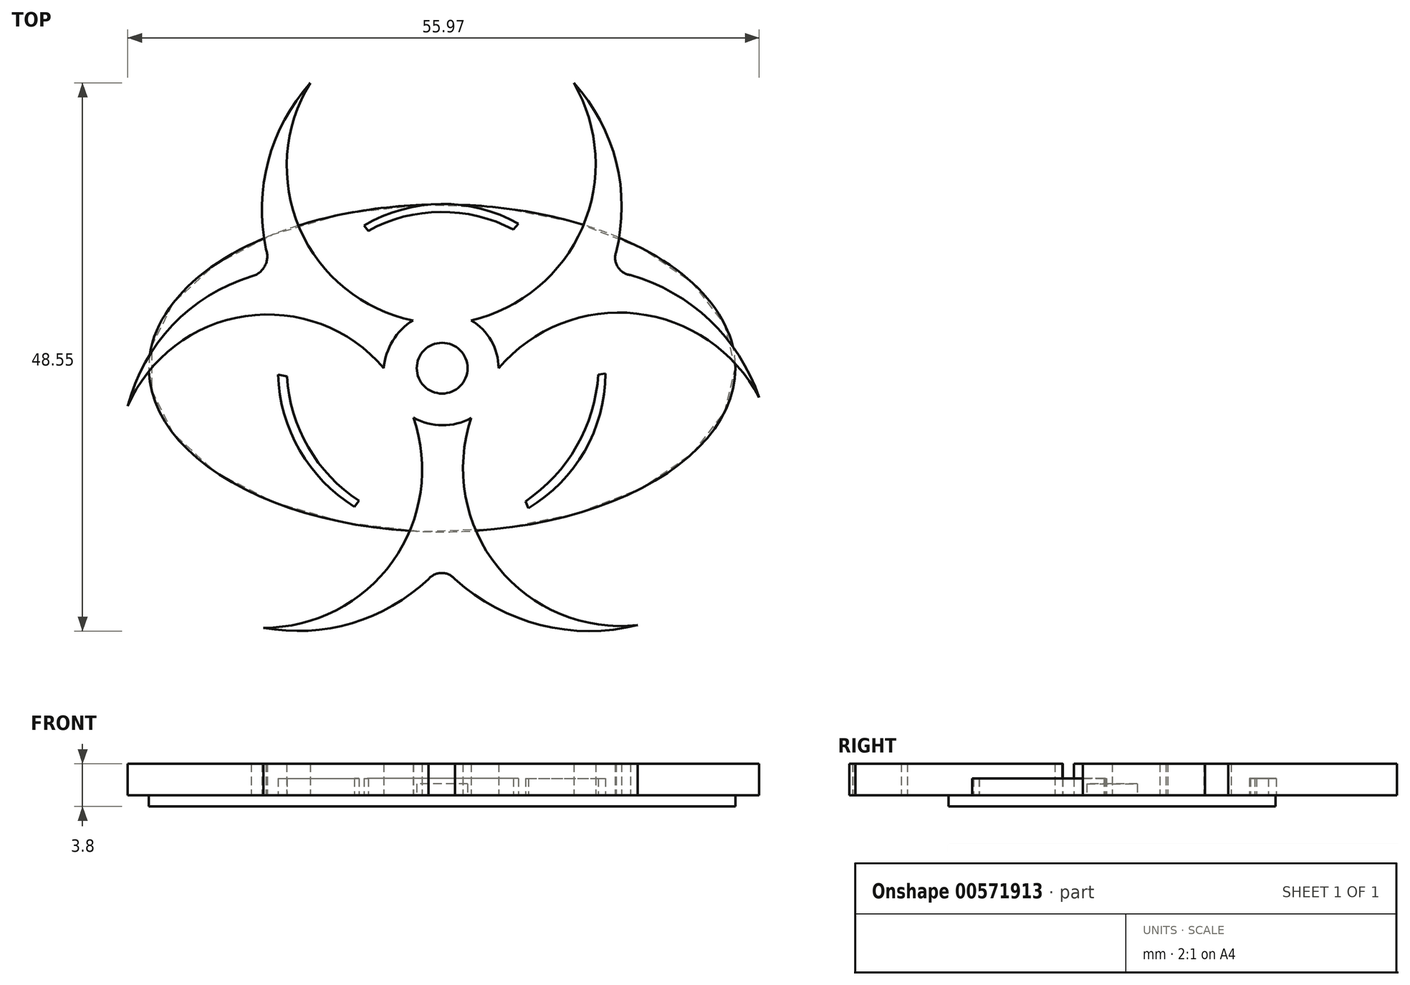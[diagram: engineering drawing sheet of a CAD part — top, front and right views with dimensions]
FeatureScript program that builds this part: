
annotation { "Feature Type Name" : "Feature", "Feature Type Description" : "" }
export const myFeature = defineFeature(function(context is Context, id is Id, definition is map)
    precondition{}
    {
        {
            var Q0;
            Q0=qCreatedBy(makeId("Top.planeOp"),FACE);
            var sketch = newSketch(context, id + "F0", { "sketchPlane" : qUnion([Q0])});
            skCircle(sketch, "E0", {"center": v(0, 0) * mm, "radius": 2.5 * mm});
            skArc(sketch, "E1", {"start": v(-16.91, 8.13) * mm, "mid": v(-15.72, 9.05) * mm, "end": v(-15.61, 10.55) * mm});
            skArc(sketch, "E2", {"start": v(-16.91, 8.13) * mm, "mid": v(-23.9, 3.81) * mm, "end": v(-27.87, -3.37) * mm});
            skArc(sketch, "E3", {"start": v(-5.17, 0) * mm, "mid": v(-17.45, 4.61) * mm, "end": v(-27.87, -3.37) * mm});
            skArc(sketch, "E4", {"start": v(-2.58, 4.24) * mm, "mid": v(-4.38, 2.43) * mm, "end": v(-5.17, 0) * mm});
            skArc(sketch, "E5", {"start": v(-11.69, 25.26) * mm, "mid": v(-15.41, 18.38) * mm, "end": v(-15.61, 10.55) * mm});
            skArc(sketch, "E6", {"start": v(-11.69, 25.26) * mm, "mid": v(-12.63, 12.37) * mm, "end": v(-2.58, 4.24) * mm});
            skArc(sketch, "E7", {"start": v(5, 0) * mm, "mid": v(4.35, 2.44) * mm, "end": v(2.57, 4.24) * mm});
            skArc(sketch, "E8", {"start": v(28.1, -2.6) * mm, "mid": v(23.74, 4.23) * mm, "end": v(16.7, 8.24) * mm});
            skArc(sketch, "E9", {"start": v(28.1, -2.6) * mm, "mid": v(17.24, 4.84) * mm, "end": v(5, 0) * mm});
            skArc(sketch, "E10", {"start": v(15.41, 10.29) * mm, "mid": v(15.58, 8.96) * mm, "end": v(16.7, 8.24) * mm});
            skArc(sketch, "E11", {"start": v(15.41, 10.29) * mm, "mid": v(15.43, 18.25) * mm, "end": v(11.67, 25.26) * mm});
            skArc(sketch, "E12", {"start": v(2.57, 4.24) * mm, "mid": v(12.43, 12.45) * mm, "end": v(11.67, 25.26) * mm});
            skArc(sketch, "E13", {"start": v(1.14, -18.7) * mm, "mid": v(8.73, -22.76) * mm, "end": v(17.34, -22.76) * mm});
            skArc(sketch, "E14", {"start": v(-2.55, -4.38) * mm, "mid": v(0.01, -5.06) * mm, "end": v(2.58, -4.41) * mm});
            skArc(sketch, "E15", {"start": v(1.14, -18.7) * mm, "mid": v(-0.04, -18.15) * mm, "end": v(-1.21, -18.7) * mm});
            skArc(sketch, "E16", {"start": v(-15.84, -23) * mm, "mid": v(-8.01, -22.6) * mm, "end": v(-1.21, -18.7) * mm});
            skArc(sketch, "E17", {"start": v(-15.84, -23) * mm, "mid": v(-4.39, -17.12) * mm, "end": v(-2.55, -4.38) * mm});
            skArc(sketch, "E18", {"start": v(2.58, -4.41) * mm, "mid": v(4.94, -17.63) * mm, "end": v(17.34, -22.76) * mm});
            skArc(sketch, "E19", {"start": v(7.39, -11.8) * mm, "mid": v(11.91, -6.93) * mm, "end": v(13.84, -0.56) * mm});
            skArc(sketch, "E20", {"start": v(7.64, -12.4) * mm, "mid": v(12.63, -7.35) * mm, "end": v(14.47, -0.49) * mm});
            skLineSegment(sketch, "E21", {"start": v(13.84, -0.56) * mm, "end": v(14.47, -0.49) * mm});
            skLineSegment(sketch, "E22", {"start": v(7.39, -11.8) * mm, "end": v(7.64, -12.4) * mm});
            skArc(sketch, "E23", {"start": v(-13.76, -0.72) * mm, "mid": v(-11.87, -7) * mm, "end": v(-7.37, -11.76) * mm});
            skArc(sketch, "E24", {"start": v(-14.54, -0.58) * mm, "mid": v(-12.63, -7.28) * mm, "end": v(-7.78, -12.27) * mm});
            skLineSegment(sketch, "E25", {"start": v(-14.54, -0.58) * mm, "end": v(-13.76, -0.72) * mm});
            skLineSegment(sketch, "E26", {"start": v(-7.37, -11.76) * mm, "end": v(-7.78, -12.27) * mm});
            skArc(sketch, "E27", {"start": v(6.78, 12.8) * mm, "mid": v(-0.1, 14.55) * mm, "end": v(-6.92, 12.64) * mm});
            skArc(sketch, "E28", {"start": v(6.33, 12.28) * mm, "mid": v(-0.13, 13.85) * mm, "end": v(-6.56, 12.18) * mm});
            skLineSegment(sketch, "E29", {"start": v(-6.92, 12.64) * mm, "end": v(-6.56, 12.18) * mm});
            skLineSegment(sketch, "E30", {"start": v(6.78, 12.8) * mm, "end": v(6.33, 12.28) * mm});
            skSolve(sketch);
        }
        {
            var Q0;
            Q0=makeQuery(id+"F0.imprint","IMPRINT",FACE,{"disambiguationData":[TD([[makeQuery(id+"F0.imprint","IMPRINT",EDGE,{"derivedFrom":sQuery(id+"F0.wireOp",EDGE,"E7")}),-1.0]])]});
            var Q1;
            Q1=makeQuery(id+"F0.imprint","IMPRINT",FACE,{"disambiguationData":[TD([[makeQuery(id+"F0.imprint","IMPRINT",EDGE,{"derivedFrom":sQuery(id+"F0.wireOp",EDGE,"E13")}),1.0]])]});
            var Q2;
            Q2=makeQuery(id+"F0.imprint","IMPRINT",FACE,{"disambiguationData":[TD([[makeQuery(id+"F0.imprint","IMPRINT",EDGE,{"derivedFrom":sQuery(id+"F0.wireOp",EDGE,"E1")}),-1.0]])]});
            extrude(context, id + "F1", {"entities" : qUnion([Q0, Q1, Q2]), "depth" : 2.8 * mm, "offsetDistance" : 25 * mm});
        }
        {
            var Q0;
            Q0=makeQuery(id+"F0.imprint","IMPRINT",FACE,{"disambiguationData":[TD([[makeQuery(id+"F0.imprint","IMPRINT",EDGE,{"derivedFrom":sQuery(id+"F0.wireOp",EDGE,"E27")}),1.0]])]});
            var Q1;
            Q1=makeQuery(id+"F0.imprint","IMPRINT",FACE,{"disambiguationData":[TD([[makeQuery(id+"F0.imprint","IMPRINT",EDGE,{"derivedFrom":sQuery(id+"F0.wireOp",EDGE,"E23")}),-1.0]])]});
            var Q2;
            Q2=makeQuery(id+"F0.imprint","IMPRINT",FACE,{"disambiguationData":[TD([[makeQuery(id+"F0.imprint","IMPRINT",EDGE,{"derivedFrom":sQuery(id+"F0.wireOp",EDGE,"E19")}),-1.0]])]});
            extrude(context, id + "F2", {"entities" : qUnion([Q0, Q1, Q2]), "depth" : 1.5 * mm, "offsetDistance" : 25 * mm});
        }
        {
            var Q0;
            Q0=qCreatedBy(makeId("Top.planeOp"),FACE);
            var sketch = newSketch(context, id + "F3", { "sketchPlane" : qUnion([Q0])});
            skCircle(sketch, "E31", {"center": v(0, 0) * mm, "radius": 2.25 * mm});
            skSolve(sketch);
        }
        {
            var Q0;
            Q0 = qSketchRegion(id + "F3", true);
            extrude(context, id + "F4", {"entities" : qUnion([Q0]), "depth" : 1 * mm, "offsetDistance" : 25 * mm});
        }
        {
            var Q0;
            Q0=qCreatedBy(makeId("Top.planeOp"),FACE);
            var sketch = newSketch(context, id + "F5", { "sketchPlane" : qUnion([Q0])});
            skEllipse(sketch, "E32", {"center": v(0, 0) * mm, "majorRadius": 26 * mm, "minorRadius": 14.5 * mm, "majorAxis": v(1, 0)});
            skSolve(sketch);
        }
        {
            var Q0;
            Q0 = qSketchRegion(id + "F5", true);
            extrude(context, id + "F6", {"entities" : qUnion([Q0]), "operationType" : NewBodyOperationType.ADD, "oppositeDirection" : true, "depth" : 1 * mm, "offsetDistance" : 25 * mm});
        }
    });
